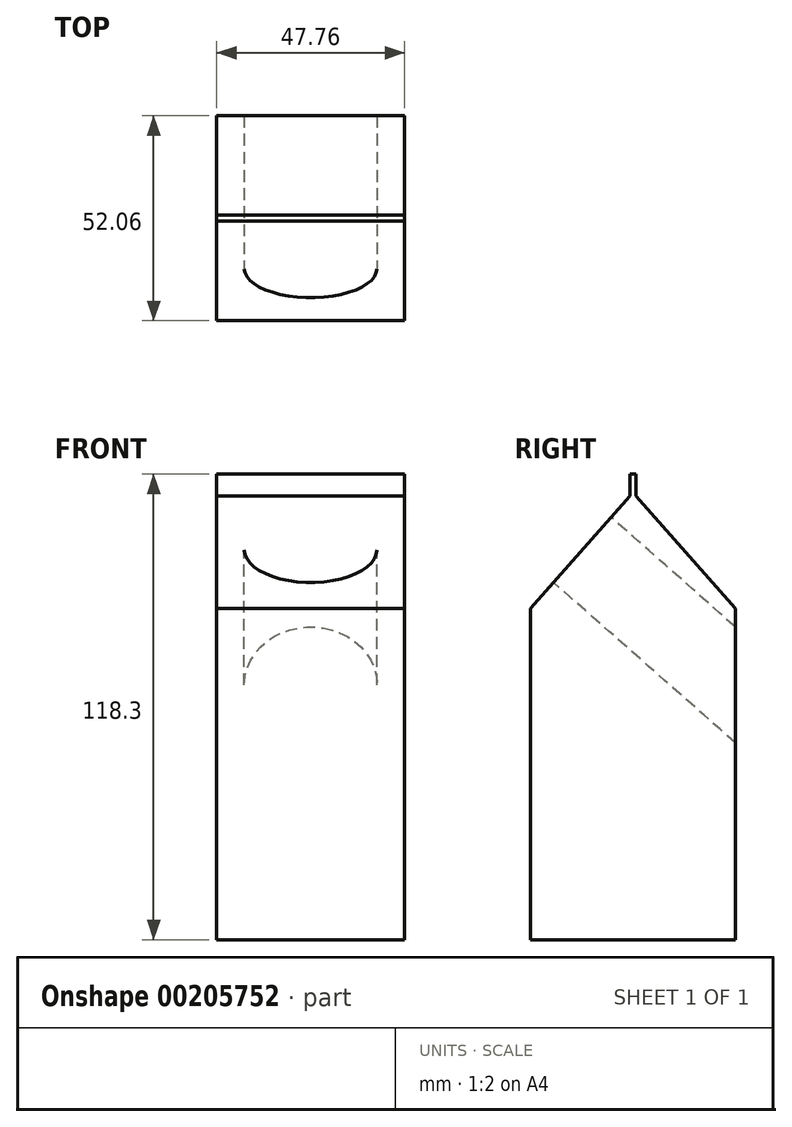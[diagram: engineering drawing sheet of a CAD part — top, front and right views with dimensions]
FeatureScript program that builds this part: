
annotation { "Feature Type Name" : "Feature", "Feature Type Description" : "" }
export const myFeature = defineFeature(function(context is Context, id is Id, definition is map)
    precondition{}
    {
        {
            var Q0;
            Q0=qCreatedBy(makeId("Right.planeOp"),FACE);
            var sketch = newSketch(context, id + "F0", { "sketchPlane" : qUnion([Q0])});
            skLineSegment(sketch, "E0.top", {"start": v(-26.03, -42.07) * mm, "end": v(26.03, -42.07) * mm});
            skLineSegment(sketch, "E0.left", {"start": v(-26.03, 42.07) * mm, "end": v(-26.03, -42.07) * mm});
            skLineSegment(sketch, "E0.right", {"start": v(26.03, 42.07) * mm, "end": v(26.03, -42.07) * mm});
            skPoint(sketch, "E0.middle", {"position": v(0, 0) * mm});
            skLineSegment(sketch, "E1", {"start": v(26.03, 42.07) * mm, "end": v(0.77, 70.71) * mm});
            skLineSegment(sketch, "E2", {"start": v(0.77, 76.23) * mm, "end": v(0.77, 70.71) * mm});
            skLineSegment(sketch, "E3", {"start": v(0.77, 76.23) * mm, "end": v(0, 76.23) * mm});
            skLineSegment(sketch, "E4.MirrorCS", {"start": v(-26.03, 42.07) * mm, "end": v(-0.77, 70.71) * mm});
            skLineSegment(sketch, "E5.MirrorCS", {"start": v(-0.77, 76.23) * mm, "end": v(-0.77, 70.71) * mm});
            skLineSegment(sketch, "E6.MirrorCS", {"start": v(-0.77, 76.23) * mm, "end": v(0, 76.23) * mm});
            skSolve(sketch);
        }
        {
            var Q0;
            Q0=makeQuery(id+"F0.imprint","IMPRINT",FACE,{"disambiguationData":[TD([[makeQuery(id+"F0.imprint","IMPRINT",EDGE,{"derivedFrom":sQuery(id+"F0.wireOp",EDGE,"E0.top")}),1.0]])]});
            extrude(context, id + "F1", {"entities" : qUnion([Q0]), "endBound" : BoundingType.SYMMETRIC, "depth" : 47.75 * mm});
        }
        {
            var Q0;
            Q0=makeQuery(id+"F1.opExtrude","SWEPT_FACE",FACE,{"disambiguationData":[OSD([sQuery(id+"F0.wireOp",EDGE,"E4.MirrorCS")])]});
            var sketch = newSketch(context, id + "F2", { "sketchPlane" : qUnion([Q0])});
            skEllipse(sketch, "E7", {"center": v(0, 34.2) * mm, "majorRadius": 16.88 * mm, "minorRadius": 11.05 * mm, "majorAxis": v(-1, 0)});
            skSolve(sketch);
        }
        {
            var Q0;
            Q0=makeQuery(id+"F2.imprint","IMPRINT",FACE,{"disambiguationData":[TD([[makeQuery(id+"F2.imprint","IMPRINT",EDGE,{"derivedFrom":sQuery(id+"F2.wireOp",EDGE,"E7")}),1.0]])]});
            extrude(context, id + "F3", {"entities" : qUnion([Q0]), "operationType" : NewBodyOperationType.REMOVE, "oppositeDirection" : true, "depth" : 89.4 * mm});
        }
    });
